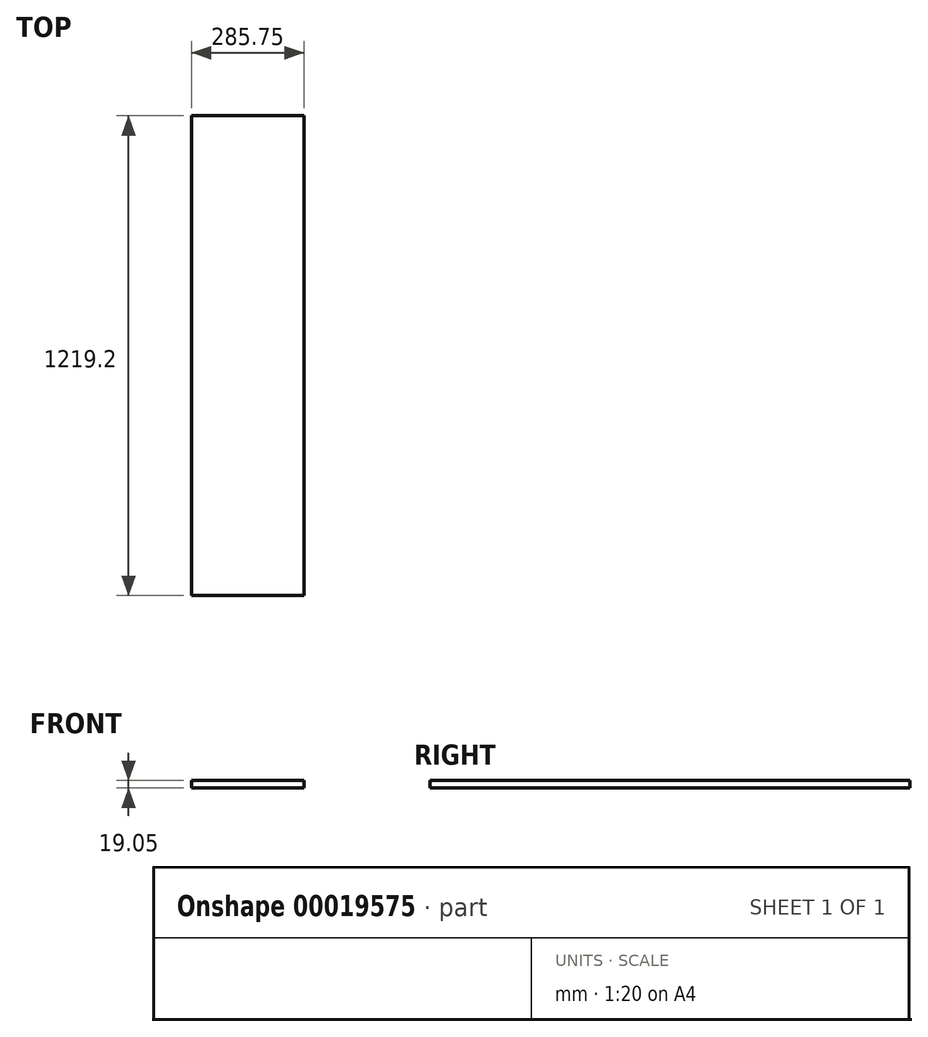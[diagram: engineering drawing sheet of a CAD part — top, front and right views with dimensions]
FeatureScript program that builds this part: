
annotation { "Feature Type Name" : "Feature", "Feature Type Description" : "" }
export const myFeature = defineFeature(function(context is Context, id is Id, definition is map)
    precondition{}
    {
        {
            var Q0;
            Q0=qCreatedBy(makeId("Top.planeOp"),FACE);
            var sketch = newSketch(context, id + "F0", { "sketchPlane" : qUnion([Q0])});
            skLineSegment(sketch, "E0.bottom", {"start": v(0, 0) * mm, "end": v(285.75, 0) * mm});
            skLineSegment(sketch, "E0.top", {"start": v(0, -1219.2) * mm, "end": v(285.75, -1219.2) * mm});
            skLineSegment(sketch, "E0.left", {"start": v(0, 0) * mm, "end": v(0, -1219.2) * mm});
            skLineSegment(sketch, "E0.right", {"start": v(285.75, 0) * mm, "end": v(285.75, -1219.2) * mm});
            skSolve(sketch);
        }
        {
            var Q0;
            Q0=makeQuery(id+"F0.imprint","IMPRINT",FACE,{"disambiguationData":[TD([[makeQuery(id+"F0.imprint","IMPRINT",EDGE,{"derivedFrom":sQuery(id+"F0.wireOp",EDGE,"E0.bottom")}),-1.0]])]});
            extrude(context, id + "F1", {"entities" : qUnion([Q0]), "depth" : 19.05 * mm});
        }
    });
